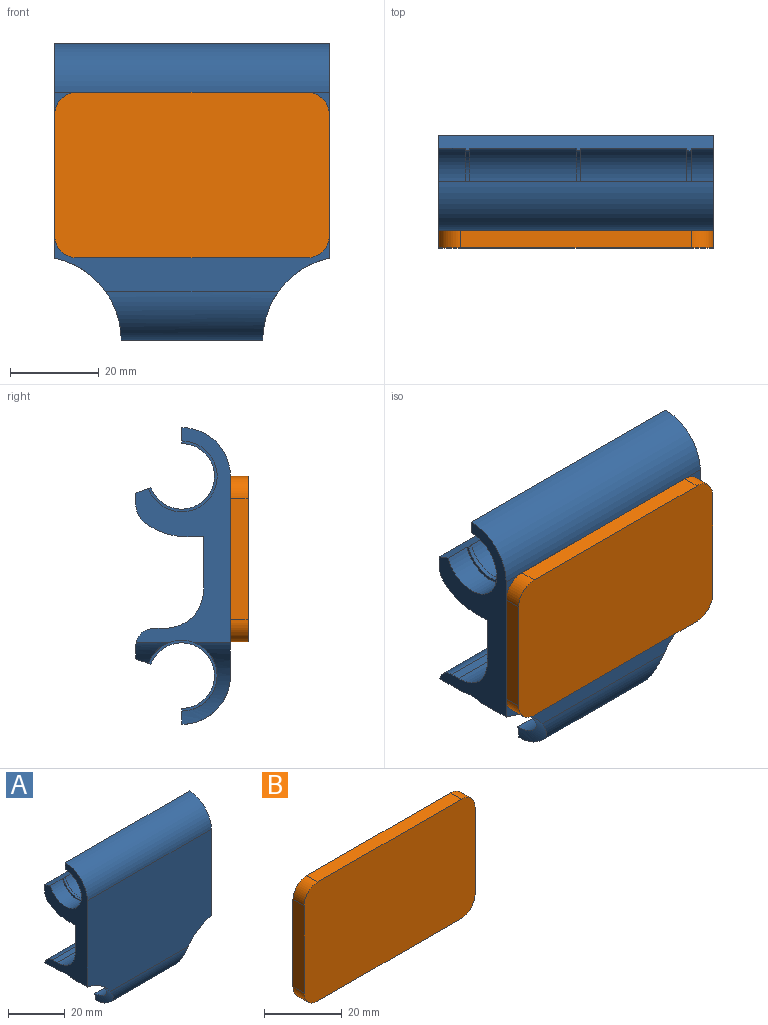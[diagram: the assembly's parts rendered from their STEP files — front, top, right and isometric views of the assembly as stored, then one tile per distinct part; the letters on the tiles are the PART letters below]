
ASSEMBLY  parts=2 mates=1
PART A: 45 faces, bbox 62.1x21.4x67.1 mm
  f0: plane 48.43x21.34mm, normal (-1,0,0), area 410.4mm2, adj f4,f7,f8,f9,f11,f12,f15,f16
  f1: plane 48.43x21.34mm, normal (1,0,0), area 410.4mm2, adj f6,f7,f8,f9,f10,f11,f12,f13
  f2: plane 55.93x2.89mm, normal (0,1,0), area 145.6mm2, adj f13,f15,f21,f42
  f3: cylinder r=8mm len=24mm, axis (-1,0,0), area 837.8mm2, adj f9,f11,f30,f35
  f4: cylinder r=8mm len=16mm, axis (-1,0,0), area 209.4mm2, adj f0,f9,f11,f32
  f5: cylinder r=8mm len=24mm, axis (-1,0,0), area 837.8mm2, adj f9,f11,f29,f33
  f6: cylinder r=8mm len=20.2mm, axis (-1,0,0), area 432.2mm2, adj f1,f13,f14,f20,f21,f23
  f7: plane 62x2.68mm, normal (0,1,0), area 166.2mm2, adj f0,f1,f9,f41
  f8: plane 62x45mm, normal (0,-1,0), area 2679.1mm2, adj f0,f1,f12,f14,f16,f19
  f9: plane 62x3.38mm, normal (0,0.34,0.94), area 187.8mm2, adj f0,f1,f3,f4,f5,f7,f10,f28
  f10: cylinder r=8mm len=16mm, axis (-1,0,0), area 174.5mm2, adj f1,f9,f11,f36
  f11: plane 62x3.6mm, normal (0,1,0), area 187.8mm2, adj f0,f1,f3,f4,f5,f10,f12,f28
  f12: cylinder r=11mm len=62mm, axis (-1,0,0), area 1071.3mm2, adj f0,f1,f8,f11
  f13: cylinder r=19mm len=9.13mm, axis (0,1,0), area 49.7mm2, adj f1,f2,f6,f21,f42
  f14: cylinder r=19mm len=18.57mm, axis (0,1,0), area 117.6mm2, adj f1,f6,f8,f19,f20
  f15: cylinder r=19mm len=9.13mm, axis (0,-1,0), area 49.7mm2, adj f0,f2,f17,f21,f42
  f16: cylinder r=19mm len=18.57mm, axis (0,-1,0), area 117.6mm2, adj f0,f8,f17,f19,f20
  f17: cylinder r=8mm len=20.6mm, axis (-1,0,0), area 446.2mm2, adj f0,f15,f16,f20,f21,f27
  f18: cylinder r=8mm len=19.2mm, axis (-1,0,0), area 670.2mm2, adj f20,f21,f24,f26
  f19: cylinder r=11mm len=39.02mm, axis (-1,0,0), area 579.3mm2, adj f8,f14,f16,f20
  f20: plane 32.48x3.6mm, normal (0,1,0), area 97.7mm2, adj f6,f14,f16,f17,f18,f19,f22,f23
  f21: plane 46.14x3.45mm, normal (0,0.34,-0.94), area 135.8mm2, adj f2,f6,f13,f15,f17,f18,f22,f23
  f22: cylinder r=7.4mm len=14.8mm, axis (-1,0,0), area 32.3mm2, adj f20,f21,f23,f24
  f23: plane 16x15.52mm, normal (1,0,0), area 20.2mm2, adj f6,f20,f21,f22
  f24: plane 16x15.52mm, normal (-1,0,0), area 20.2mm2, adj f18,f20,f21,f22
  f25: cylinder r=7.4mm len=14.8mm, axis (-1,0,0), area 32.3mm2, adj f20,f21,f26,f27
  f26: plane 16x15.52mm, normal (1,0,0), area 20.2mm2, adj f18,f20,f21,f25
  f27: plane 16x15.52mm, normal (-1,0,0), area 20.2mm2, adj f17,f20,f21,f25
  f28: cylinder r=7.4mm len=14.8mm, axis (1,0,0), area 32.3mm2, adj f9,f11,f29,f30
  f29: plane 16x15.52mm, normal (-1,0,0), area 20.2mm2, adj f5,f9,f11,f28
  f30: plane 16x15.52mm, normal (1,0,0), area 20.2mm2, adj f3,f9,f11,f28
  f31: cylinder r=7.4mm len=14.8mm, axis (1,0,0), area 32.3mm2, adj f9,f11,f32,f33
  f32: plane 16x15.52mm, normal (-1,0,0), area 20.2mm2, adj f4,f9,f11,f31
  f33: plane 16x15.52mm, normal (1,0,0), area 20.2mm2, adj f5,f9,f11,f31
  f34: cylinder r=7.4mm len=14.8mm, axis (1,0,0), area 32.3mm2, adj f9,f11,f35,f36
  f35: plane 16x15.52mm, normal (-1,0,0), area 20.2mm2, adj f3,f9,f11,f34
  f36: plane 16x15.52mm, normal (1,0,0), area 20.2mm2, adj f9,f10,f11,f34
  f37: plane 62x2.19mm, normal (0,0,1), area 136.1mm2, adj f0,f1,f42,f44
  f38: plane 62x11.56mm, normal (0,1,0), area 716.6mm2, adj f0,f1,f39,f43
  f39: plane 62x3.8mm, normal (0,0,-1), area 235.7mm2, adj f0,f1,f38,f40
  f40: cylinder r=15.78mm len=62mm, axis (-1,0,0), area 637.3mm2, adj f0,f1,f39,f41
  f41: cylinder r=5mm len=62mm, axis (-1,0,0), area 285mm2, adj f0,f1,f7,f40
  f42: cylinder r=4mm len=62mm, axis (-1,0,0), area 386.5mm2, adj f0,f1,f2,f13,f15,f37
  f43: cylinder r=10mm len=62mm, axis (-1,0,0), area 449.3mm2, adj f0,f1,f38,f44
  f44: cylinder r=10mm len=62mm, axis (1,0,0), area 449.3mm2, adj f0,f1,f37,f43
PART B: 10 faces, bbox 62x4x37.4 mm
  f0: plane 27.4x4mm, normal (-1,0,0), area 109.6mm2, adj f2,f3,f7,f8
  f1: plane 27.4x4mm, normal (1,0,0), area 109.6mm2, adj f2,f3,f6,f9
  f2: plane 62x37.4mm, normal (0,-1,0), area 2297.3mm2, adj f0,f1,f4,f5,f6,f7,f8,f9
  f3: plane 62x37.4mm, normal (0,1,0), area 2297.3mm2, adj f0,f1,f4,f5,f6,f7,f8,f9
  f4: plane 52x4mm, normal (0,0,1), area 208mm2, adj f2,f3,f8,f9
  f5: plane 52x4mm, normal (0,0,-1), area 208mm2, adj f2,f3,f6,f7
  f6: cylinder r=5mm len=5mm, axis (0,-1,0), area 31.4mm2, adj f1,f2,f3,f5
  f7: cylinder r=5mm len=5mm, axis (0,1,0), area 31.4mm2, adj f0,f2,f3,f5
  f8: cylinder r=5mm len=5mm, axis (0,-1,0), area 31.4mm2, adj f0,f2,f3,f4
  f9: cylinder r=5mm len=5mm, axis (0,1,0), area 31.4mm2, adj f1,f2,f3,f4
PLACE A t=(-41.42,7.74,-1.19)mm
PLACE B t=(-37.42,-3.26,11.31)mm
MATE fastened B.f3 <-> A.f8  axis (0,1,0) through (-6.42,-3.26,21.31)mm
